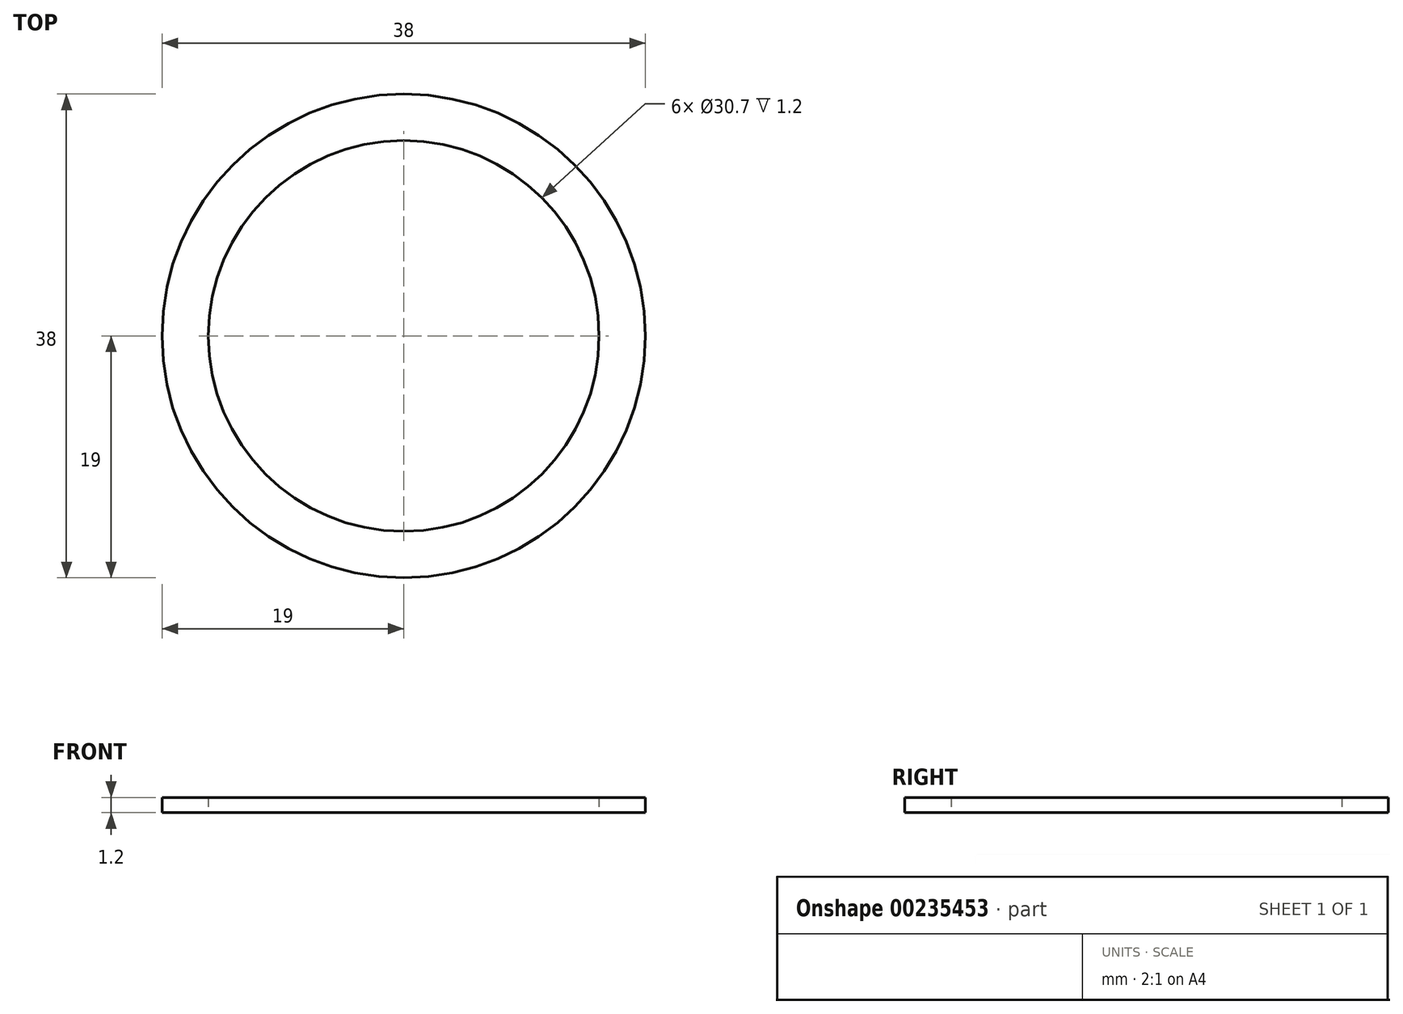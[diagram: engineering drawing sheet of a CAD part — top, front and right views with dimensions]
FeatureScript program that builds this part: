
annotation { "Feature Type Name" : "Feature", "Feature Type Description" : "" }
export const myFeature = defineFeature(function(context is Context, id is Id, definition is map)
    precondition{}
    {
        {
            var Q0;
            Q0=qCreatedBy(makeId("Top.planeOp"),FACE);
            var sketch = newSketch(context, id + "F0", { "sketchPlane" : qUnion([Q0])});
            skCircle(sketch, "E0", {"center": v(0, 0) * mm, "radius": 15.35 * mm});
            skCircle(sketch, "E1", {"center": v(0, 0) * mm, "radius": 19 * mm});
            skSolve(sketch);
        }
        {
            var Q0;
            Q0 = qSketchRegion(id + "F0", true);
            extrude(context, id + "F1", {"entities" : qUnion([Q0]), "depth" : 1.2 * mm});
        }
    });
